# Revit family: tree_
name_source: partatom
category: Furniture
revit_build: Autodesk Revit 2015 (Build: 20140903_1530(x64)
units: mm (PartAtom-declared; Revit-internal decimal feet)

## types (10) — shared parameters
BIMobject category = Furniture
Date of publishing = 2016-03-22
Design country = Sweden
Edition number = 1
IFC Classification = Furnishing Element
Manufacturer country = Sweden
Manufacturer name = Swedese
Material main = Wood
Nominal height = 1940
Nominal width = 890
OmniClass Code = 23-21 11 00
OmniClass Description = Commercial Furniture
Product Guid = 8a2fa09d-40bd-4067-8254-de45f052ca93
Product SKU = 26330
Product data url = https://bimobject.com
Product family = Accessories
Product group = Tree
Product name = Tree
QR code = http://bimobject.com
Technical description = https://static-swedese.s3.amazonaws.com
UNSPSC Code = 56
Uniclass 1.4 Code = L8211
Uniclass 1.4 Description = Furniture
Weight Net (Kg) = 19
zero-valued in all types: BOSUseNativeGeometries

## per-type parameters (varying)
| type | Height 194 | height 134 |
| TYPE - (Tree 194) COLOUR - (Orange) | Yes | No |
| TYPE - (Tree 134) COLOUR - (Orange) | No | Yes |
| TYPE - (Tree 194) COLOUR - (Pink) | Yes | No |
| TYPE - (Tree 134) COLOUR - (Pink) | No | Yes |
| TYPE - (Tree 194) COLOUR - (Grey) | Yes | No |
| TYPE - (Tree 134) COLOUR - (Grey) | No | Yes |
| TYPE - (Tree 194) COLOUR - (Blue) | Yes | No |
| TYPE - (Tree 134) COLOUR - (Blue) | Yes | No |
| TYPE - (Tree 194) COLOUR - (Yellow) | Yes | No |
| TYPE - (Tree 134) COLOUR - (Yellow) | No | Yes |

## geometry (parser evidence)
native form markers: Sweep x2
no freeform markers — native parametric forms only
